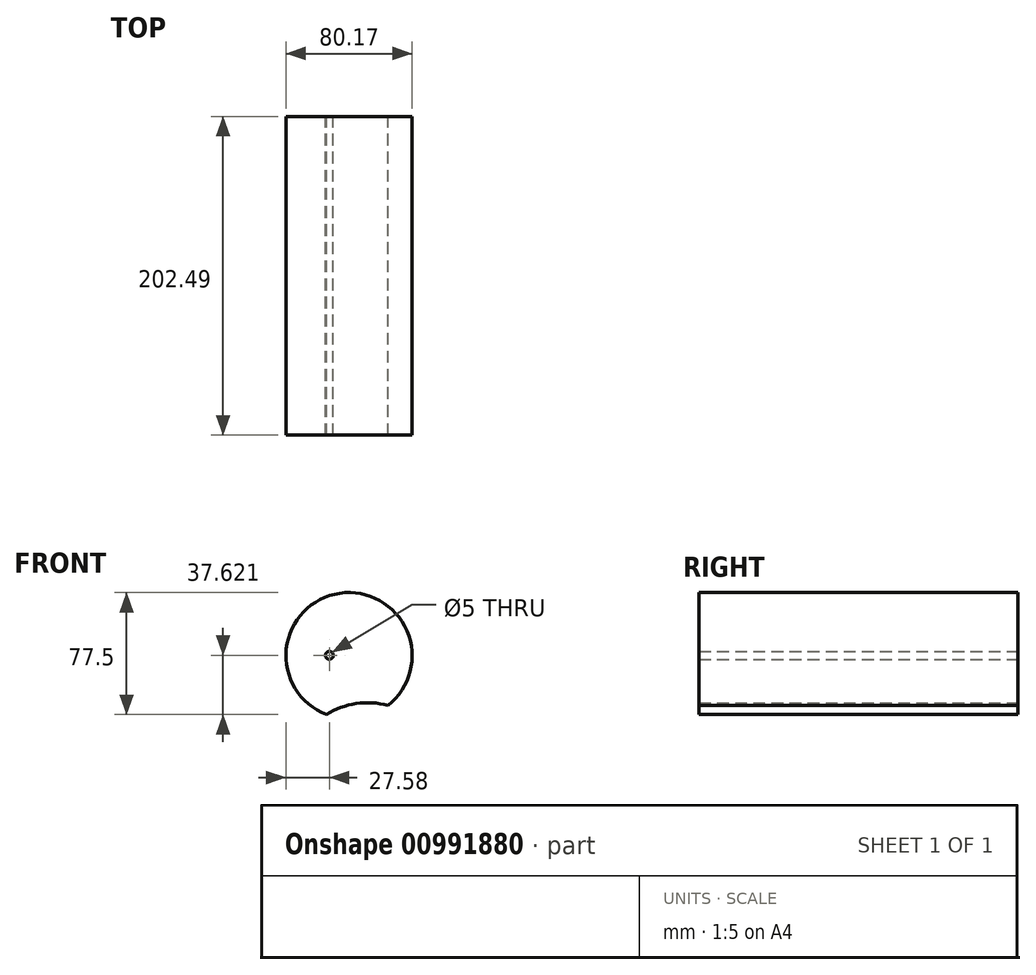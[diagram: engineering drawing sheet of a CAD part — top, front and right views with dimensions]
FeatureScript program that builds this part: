
annotation { "Feature Type Name" : "Feature", "Feature Type Description" : "" }
export const myFeature = defineFeature(function(context is Context, id is Id, definition is map)
    precondition{}
    {
        {
            var Q0;
            Q0=qCreatedBy(makeId("Front.planeOp"),FACE);
            var sketch = newSketch(context, id + "F0", { "sketchPlane" : qUnion([Q0])});
            skCircle(sketch, "E0", {"center": v(12.5, 44.8) * mm, "radius": 40.09 * mm});
            skCircle(sketch, "E1", {"center": v(-39.28, -28.1) * mm, "radius": 42.8 * mm});
            skCircle(sketch, "E2", {"center": v(24.27, -34.28) * mm, "radius": 49.2 * mm});
            skSolve(sketch);
        }
        {
            var Q0;
            {var subQ0=sQuery(id+"F0.wireOp",EDGE,"E2");var subQ1=sQuery(id+"F0.wireOp",EDGE,"E0");var subQ2=makeQuery(id+"F0.imprint","INTERSECT",VERTEX,{"disambiguationData":[OD(0.0)],"derivedFrom":[subQ1,subQ0]});Q0=makeQuery(id+"F0.imprint","IMPRINT",FACE,{"disambiguationData":[TD([[makeQuery(id+"F0.imprint","IMPRINT",EDGE,{"disambiguationData":[TD([[subQ2,1.0]])],"derivedFrom":subQ1}),1.0]])]});}
            extrude(context, id + "F1", {"entities" : qUnion([Q0]), "depth" : 202.5 * mm, "offsetDistance" : 25 * mm});
        }
        {
            var Q0;
            Q0=makeQuery(id+"F1.opExtrude","CAP_FACE",FACE,{"disambiguationData":[OSD([sQuery(id+"F0.wireOp",EDGE,"E0"),sQuery(id+"F0.wireOp",EDGE,"E2")])],"isStart":true});
            var sketch = newSketch(context, id + "F2", { "sketchPlane" : qUnion([Q0])});
            skCircle(sketch, "E3", {"center": v(0, 45) * mm, "radius": 14.14 * mm});
            skSolve(sketch);
        }
        {
            var Q0;
            Q0=sQuery(id+"F2.wireOp",VERTEX,"E3.center");
            var Q1;
            Q1=makeQuery(id+"F1.opExtrude","SWEPT_BODY",BODY,{"disambiguationData":[OSD([sQuery(id+"F0.wireOp",EDGE,"E0"),sQuery(id+"F0.wireOp",EDGE,"E2")])]});
            hole(context, id + "F3", {"style" : HoleStyle.SIMPLE, "endStyle" : HoleEndStyle.THROUGH, "holeDiameter" : 5 * mm, "majorDiameter" : 5 * mm, "isTappedThrough" : true, "tappedDepth" : 12 * mm, "tapClearance" : 3, "locations" : qUnion([Q0]), "scope" : qUnion([Q1])});
        }
    });
